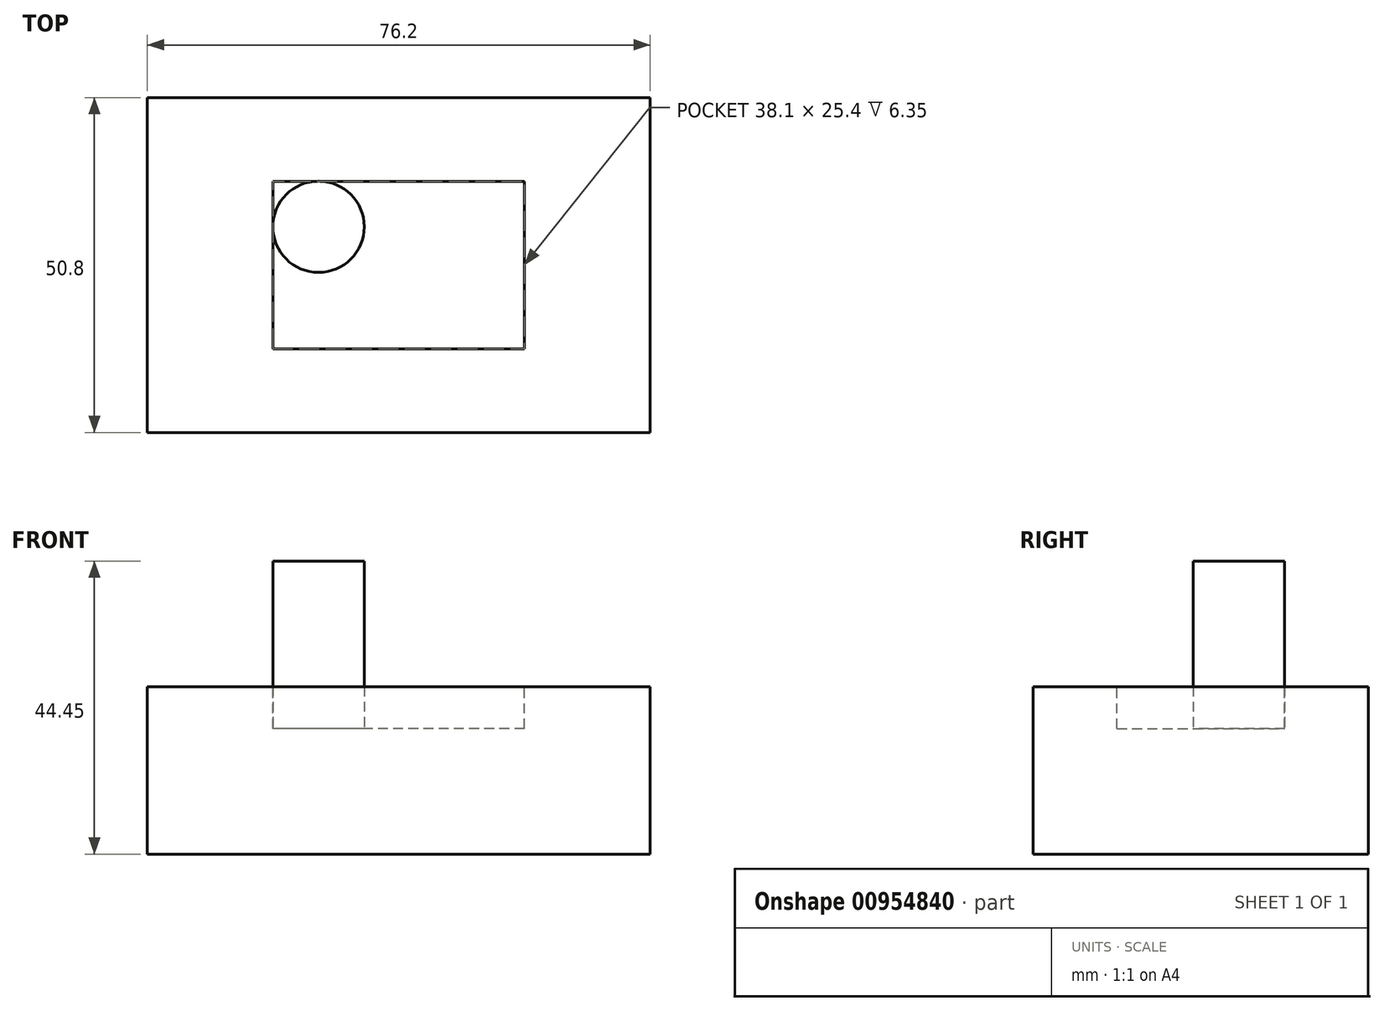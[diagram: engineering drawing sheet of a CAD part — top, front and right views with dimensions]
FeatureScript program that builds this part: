
annotation { "Feature Type Name" : "Feature", "Feature Type Description" : "" }
export const myFeature = defineFeature(function(context is Context, id is Id, definition is map)
    precondition{}
    {
        {
            var Q0;
            Q0=qCreatedBy(makeId("Top.planeOp"),FACE);
            var sketch = newSketch(context, id + "F0", { "sketchPlane" : qUnion([Q0])});
            skLineSegment(sketch, "E0.bottom", {"start": v(38.1, -25.4) * mm, "end": v(-38.1, -25.4) * mm});
            skLineSegment(sketch, "E0.top", {"start": v(38.1, 25.4) * mm, "end": v(-38.1, 25.4) * mm});
            skLineSegment(sketch, "E0.left", {"start": v(38.1, -25.4) * mm, "end": v(38.1, 25.4) * mm});
            skLineSegment(sketch, "E0.right", {"start": v(-38.1, -25.4) * mm, "end": v(-38.1, 25.4) * mm});
            skPoint(sketch, "E0.middle", {"position": v(0, 0) * mm});
            skSolve(sketch);
        }
        {
            var Q0;
            Q0 = qSketchRegion(id + "F0", true);
            extrude(context, id + "F1", {"entities" : qUnion([Q0]), "depth" : 25.4 * mm, "offsetDistance" : 25.4 * mm});
        }
        {
            var Q0;
            Q0=makeQuery(id+"F1.opExtrude","CAP_FACE",FACE,{"disambiguationData":[OSD([sQuery(id+"F0.wireOp",EDGE,"E0.bottom"),sQuery(id+"F0.wireOp",EDGE,"E0.top"),sQuery(id+"F0.wireOp",EDGE,"E0.left"),sQuery(id+"F0.wireOp",EDGE,"E0.right")])],"isStart":false});
            var sketch = newSketch(context, id + "F2", { "sketchPlane" : qUnion([Q0])});
            skLineSegment(sketch, "E1.bottom", {"start": v(19.05, -12.7) * mm, "end": v(-19.05, -12.7) * mm});
            skLineSegment(sketch, "E1.top", {"start": v(19.05, 12.7) * mm, "end": v(-19.05, 12.7) * mm});
            skLineSegment(sketch, "E1.left", {"start": v(19.05, -12.7) * mm, "end": v(19.05, 12.7) * mm});
            skLineSegment(sketch, "E1.right", {"start": v(-19.05, -12.7) * mm, "end": v(-19.05, 12.7) * mm});
            skPoint(sketch, "E1.middle", {"position": v(0, 0) * mm});
            skSolve(sketch);
        }
        {
            var Q0;
            Q0=makeQuery(id+"F2.imprint","IMPRINT",FACE,{"disambiguationData":[TD([[makeQuery(id+"F2.imprint","IMPRINT",EDGE,{"derivedFrom":sQuery(id+"F2.wireOp",EDGE,"E1.bottom")}),-1.0]])]});
            extrude(context, id + "F3", {"entities" : qUnion([Q0]), "operationType" : NewBodyOperationType.REMOVE, "oppositeDirection" : true, "depth" : 6.35 * mm, "offsetDistance" : 25.4 * mm});
        }
        {
            var Q0;
            Q0=makeQuery(id+"F3.boolean.opBoolean","COPY",FACE,{"derivedFrom":makeQuery(id+"F3.opExtrude","CAP_FACE",FACE,{"disambiguationData":[OSD([sQuery(id+"F2.wireOp",EDGE,"E1.bottom"),sQuery(id+"F2.wireOp",EDGE,"E1.top"),sQuery(id+"F2.wireOp",EDGE,"E1.left"),sQuery(id+"F2.wireOp",EDGE,"E1.right")])],"isStart":false})});
            var sketch = newSketch(context, id + "F4", { "sketchPlane" : qUnion([Q0])});
            skCircle(sketch, "E2", {"center": v(-12.16, 5.78) * mm, "radius": 6.92 * mm});
            skPoint(sketch, "E2.first.point", {"position": v(-12.35, 12.7) * mm});
            skPoint(sketch, "E2.second.point", {"position": v(-19.05, 6.41) * mm});
            skPoint(sketch, "E2.third.point", {"position": v(-6.3, 2.12) * mm});
            skSolve(sketch);
        }
        {
            var Q0;
            Q0 = qSketchRegion(id + "F4", true);
            extrude(context, id + "F5", {"entities" : qUnion([Q0]), "depth" : 25.4 * mm, "offsetDistance" : 25.4 * mm});
        }
    });
